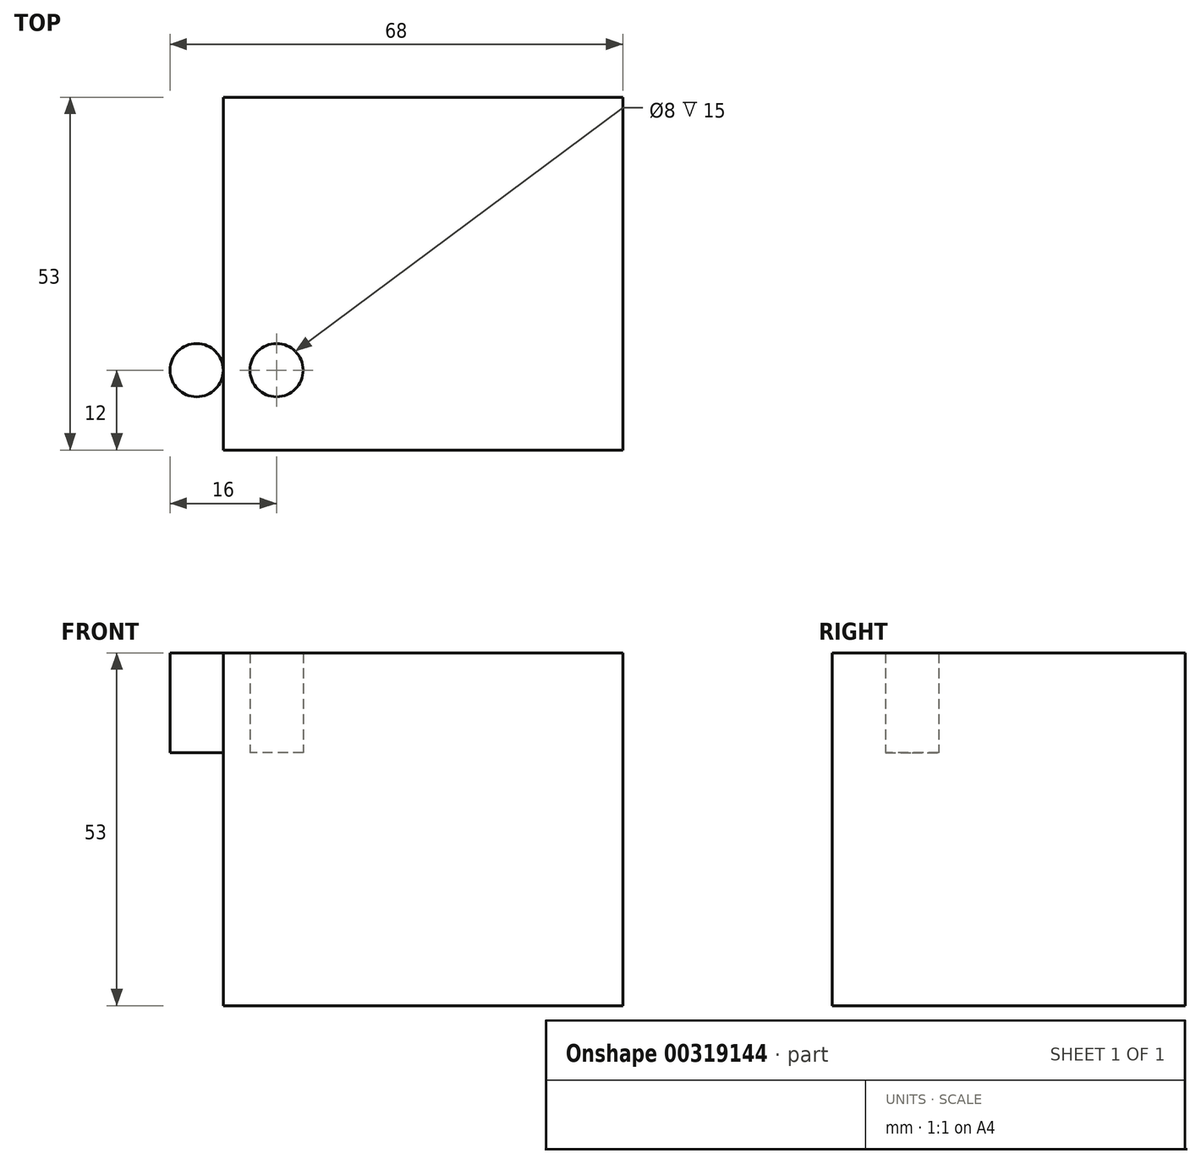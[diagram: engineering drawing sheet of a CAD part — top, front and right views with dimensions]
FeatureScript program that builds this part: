
annotation { "Feature Type Name" : "Feature", "Feature Type Description" : "" }
export const myFeature = defineFeature(function(context is Context, id is Id, definition is map)
    precondition{}
    {
        {
            var Q0;
            Q0=qCreatedBy(makeId("Top.planeOp"),FACE);
            var sketch = newSketch(context, id + "F0", { "sketchPlane" : qUnion([Q0])});
            skLineSegment(sketch, "E0.bottom", {"start": v(0, 0) * mm, "end": v(60, 0) * mm});
            skLineSegment(sketch, "E0.top", {"start": v(0, 53) * mm, "end": v(60, 53) * mm});
            skLineSegment(sketch, "E0.left", {"start": v(0, 0) * mm, "end": v(0, 53) * mm});
            skLineSegment(sketch, "E0.right", {"start": v(60, 0) * mm, "end": v(60, 53) * mm});
            skCircle(sketch, "E1", {"center": v(8, 12) * mm, "radius": 4 * mm});
            skCircle(sketch, "E2", {"center": v(-4, 12) * mm, "radius": 4 * mm});
            skPoint(sketch, "E3", {"position": v(0, 12) * mm});
            skSolve(sketch);
        }
        {
            var Q0;
            Q0=makeQuery(id+"F0.imprint","IMPRINT",FACE,{"disambiguationData":[TD([[makeQuery(id+"F0.imprint","IMPRINT",EDGE,{"derivedFrom":sQuery(id+"F0.wireOp",EDGE,"E0.bottom")}),1.0]])]});
            var Q1;
            Q1=makeQuery(id+"F0.imprint","IMPRINT",FACE,{"disambiguationData":[TD([[makeQuery(id+"F0.imprint","IMPRINT",EDGE,{"derivedFrom":sQuery(id+"F0.wireOp",EDGE,"E1")}),1.0]])]});
            extrude(context, id + "F1", {"entities" : qUnion([Q0, Q1]), "depth" : 53 * mm});
        }
        {
            var Q0;
            Q0=makeQuery(id+"F1.opExtrude","SWEPT_FACE",FACE,{"disambiguationData":[OSD([sQuery(id+"F0.wireOp",EDGE,"E0.bottom")])]});
            var sketch = newSketch(context, id + "F2", { "sketchPlane" : qUnion([Q0])});
            skPoint(sketch, "E4", {"position": v(0, 38) * mm});
            skSolve(sketch);
        }
        {
            var Q0;
            Q0=makeQuery(id+"F0.imprint","IMPRINT",FACE,{"disambiguationData":[TD([[makeQuery(id+"F0.imprint","IMPRINT",EDGE,{"derivedFrom":sQuery(id+"F0.wireOp",EDGE,"E1")}),1.0]])]});
            var Q1;
            Q1=makeQuery(id+"F0.imprint","IMPRINT",FACE,{"disambiguationData":[TD([[makeQuery(id+"F0.imprint","IMPRINT",EDGE,{"derivedFrom":sQuery(id+"F0.wireOp",EDGE,"E2")}),1.0]])]});
            var Q2;
            Q2=makeQuery(id+"F1.opExtrude","CAP_VERTEX",VERTEX,{"disambiguationData":[OSD([sQuery(id+"F0.wireOp",EDGE,"E0.bottom"),sQuery(id+"F0.wireOp",EDGE,"E0.left")])],"isStart":false});
            var Q3;
            Q3=sQuery(id+"F2.wireOp",VERTEX,"E4");
            extrude(context, id + "F3", {"entities" : qUnion([Q0, Q1]), "operationType" : NewBodyOperationType.REMOVE, "endBound" : BoundingType.UP_TO_VERTEX, "endBoundEntityVertex" : qUnion([Q2]), "depth" : 25 * mm, "hasSecondDirection" : true, "secondDirectionBound" : SecondDirectionBoundingType.UP_TO_VERTEX, "secondDirectionOppositeDirection" : false, "secondDirectionBoundEntityVertex" : qUnion([Q3]), "secondDirectionDepth" : 25 * mm});
        }
        {
            var Q0;
            Q0=makeQuery(id+"F0.imprint","IMPRINT",FACE,{"disambiguationData":[TD([[makeQuery(id+"F0.imprint","IMPRINT",EDGE,{"derivedFrom":sQuery(id+"F0.wireOp",EDGE,"E2")}),1.0]])]});
            var Q1;
            Q1=makeQuery(id+"F1.opExtrude","CAP_VERTEX",VERTEX,{"disambiguationData":[OSD([sQuery(id+"F0.wireOp",EDGE,"E0.bottom"),sQuery(id+"F0.wireOp",EDGE,"E0.left")])],"isStart":false});
            var Q2;
            Q2=sQuery(id+"F2.wireOp",VERTEX,"E4");
            extrude(context, id + "F4", {"entities" : qUnion([Q0]), "endBound" : BoundingType.UP_TO_VERTEX, "endBoundEntityVertex" : qUnion([Q1]), "depth" : 25 * mm, "hasSecondDirection" : true, "secondDirectionBound" : SecondDirectionBoundingType.UP_TO_VERTEX, "secondDirectionOppositeDirection" : false, "secondDirectionBoundEntityVertex" : qUnion([Q2]), "secondDirectionDepth" : 25 * mm});
        }
    });
